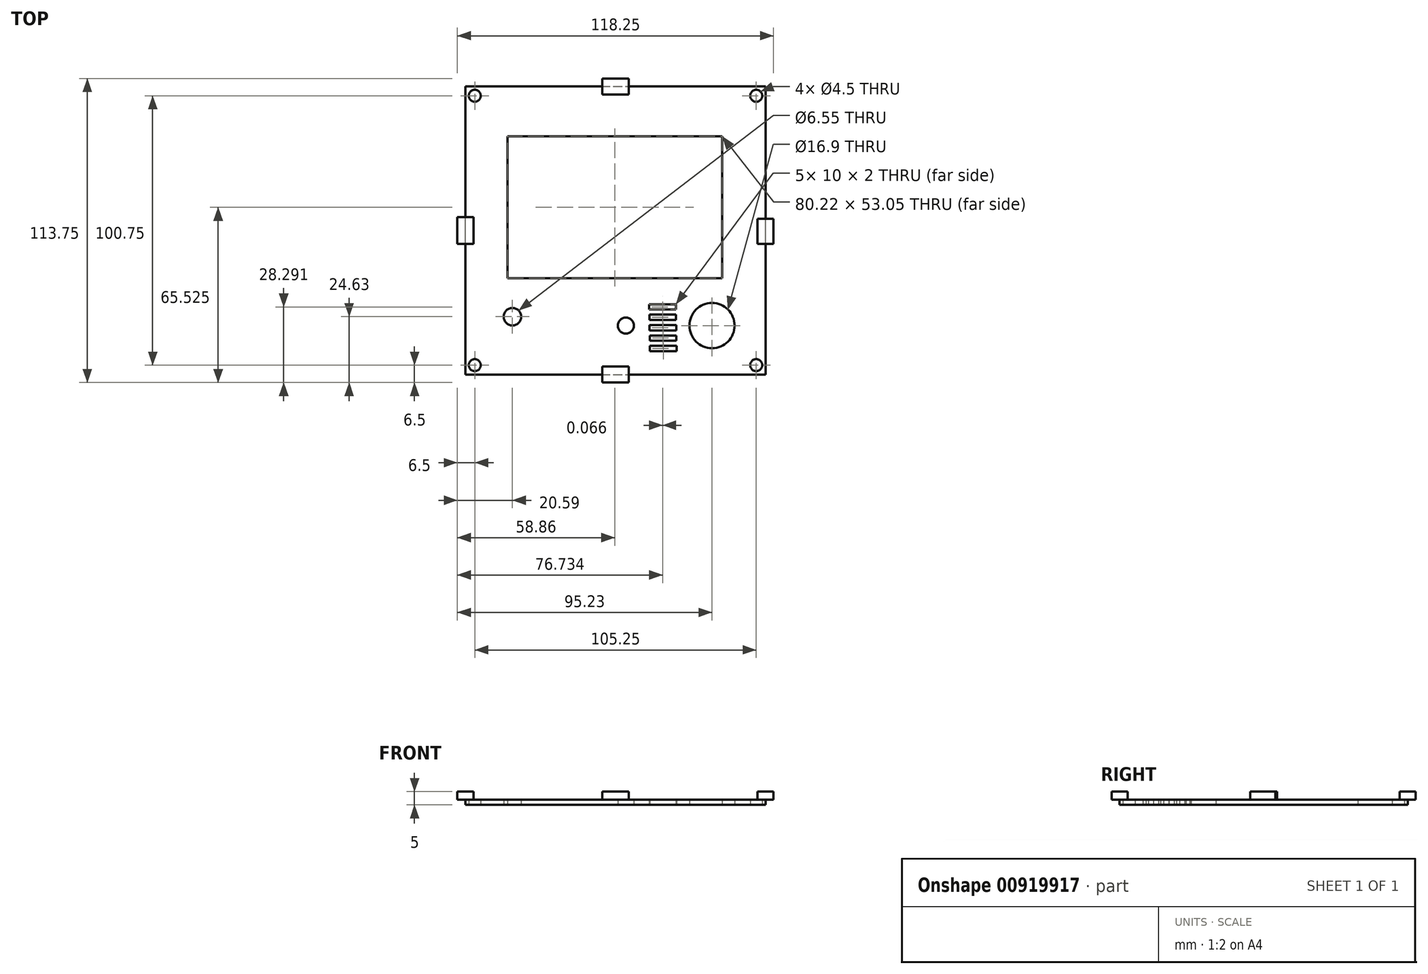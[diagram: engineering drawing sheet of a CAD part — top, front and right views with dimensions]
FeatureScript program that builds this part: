
annotation { "Feature Type Name" : "Feature", "Feature Type Description" : "" }
export const myFeature = defineFeature(function(context is Context, id is Id, definition is map)
    precondition{}
    {
        {
            var Q0;
            Q0=qCreatedBy(makeId("Top.planeOp"),FACE);
            var sketch = newSketch(context, id + "F0", { "sketchPlane" : qUnion([Q0])});
            skLineSegment(sketch, "E0.bottom", {"start": v(0, 0) * mm, "end": v(112.25, 0) * mm});
            skLineSegment(sketch, "E0.top", {"start": v(0, 107.75) * mm, "end": v(112.25, 107.75) * mm});
            skLineSegment(sketch, "E0.left", {"start": v(0, 0) * mm, "end": v(0, 107.75) * mm});
            skLineSegment(sketch, "E0.right", {"start": v(112.25, 0) * mm, "end": v(112.25, 107.75) * mm});
            skCircle(sketch, "E1", {"center": v(3.5, 104.25) * mm, "radius": 2.25 * mm});
            skCircle(sketch, "E2", {"center": v(108.75, 104.25) * mm, "radius": 2.25 * mm});
            skCircle(sketch, "E3", {"center": v(3.5, 3.5) * mm, "radius": 2.25 * mm});
            skCircle(sketch, "E4", {"center": v(108.75, 3.5) * mm, "radius": 2.25 * mm});
            skLineSegment(sketch, "E5.bottom", {"start": v(15.75, 89.05) * mm, "end": v(95.97, 89.05) * mm});
            skLineSegment(sketch, "E5.top", {"start": v(15.75, 36) * mm, "end": v(95.97, 36) * mm});
            skLineSegment(sketch, "E5.left", {"start": v(15.75, 89.05) * mm, "end": v(15.75, 36) * mm});
            skLineSegment(sketch, "E5.right", {"start": v(95.97, 89.05) * mm, "end": v(95.97, 36) * mm});
            skCircle(sketch, "E6", {"center": v(92.23, 18.3) * mm, "radius": 8.45 * mm});
            skCircle(sketch, "E7", {"center": v(60, 18.3) * mm, "radius": 3 * mm});
            skCircle(sketch, "E8", {"center": v(17.59, 21.63) * mm, "radius": 3.28 * mm});
            skLineSegment(sketch, "E9.bottom", {"start": v(68.73, 26.3) * mm, "end": v(78.73, 26.3) * mm});
            skLineSegment(sketch, "E9.top", {"start": v(68.73, 24.3) * mm, "end": v(78.73, 24.3) * mm});
            skLineSegment(sketch, "E9.left", {"start": v(68.73, 26.3) * mm, "end": v(68.73, 24.3) * mm});
            skLineSegment(sketch, "E9.right", {"start": v(78.73, 26.3) * mm, "end": v(78.73, 24.3) * mm});
            skLineSegment(sketch, "E10.1.0.0", {"start": v(78.8, 22.4) * mm, "end": v(78.8, 20.4) * mm});
            skLineSegment(sketch, "E10.1.0.1", {"start": v(68.8, 22.4) * mm, "end": v(68.8, 20.4) * mm});
            skLineSegment(sketch, "E10.1.0.2", {"start": v(68.8, 22.4) * mm, "end": v(78.8, 22.4) * mm});
            skLineSegment(sketch, "E10.1.0.3", {"start": v(68.8, 20.4) * mm, "end": v(78.8, 20.4) * mm});
            skLineSegment(sketch, "E10.2.0.0", {"start": v(78.87, 18.5) * mm, "end": v(78.87, 16.5) * mm});
            skLineSegment(sketch, "E10.2.0.1", {"start": v(68.87, 18.5) * mm, "end": v(68.87, 16.5) * mm});
            skLineSegment(sketch, "E10.2.0.2", {"start": v(68.87, 18.5) * mm, "end": v(78.87, 18.5) * mm});
            skLineSegment(sketch, "E10.2.0.3", {"start": v(68.87, 16.5) * mm, "end": v(78.87, 16.5) * mm});
            skLineSegment(sketch, "E10.3.0.0", {"start": v(78.93, 14.62) * mm, "end": v(78.93, 12.62) * mm});
            skLineSegment(sketch, "E10.3.0.1", {"start": v(68.93, 14.62) * mm, "end": v(68.93, 12.62) * mm});
            skLineSegment(sketch, "E10.3.0.2", {"start": v(68.93, 14.62) * mm, "end": v(78.93, 14.62) * mm});
            skLineSegment(sketch, "E10.3.0.3", {"start": v(68.93, 12.62) * mm, "end": v(78.93, 12.62) * mm});
            skLineSegment(sketch, "E10.4.0.0", {"start": v(79, 10.73) * mm, "end": v(79, 8.73) * mm});
            skLineSegment(sketch, "E10.4.0.1", {"start": v(69, 10.73) * mm, "end": v(69, 8.73) * mm});
            skLineSegment(sketch, "E10.4.0.2", {"start": v(69, 10.73) * mm, "end": v(79, 10.73) * mm});
            skLineSegment(sketch, "E10.4.0.3", {"start": v(69, 8.73) * mm, "end": v(79, 8.73) * mm});
            skLineSegment(sketch, "E10.direction1", {"start": v(68.73, 24.3) * mm, "end": v(68.8, 20.4) * mm, "construction": true});
            skSolve(sketch);
        }
        {
            var Q0;
            Q0=qSketchRegion(id+"F0",true);
            extrude(context, id + "F1", {"entities" : qUnion([Q0]), "depth" : 2 * mm, "offsetDistance" : 25 * mm});
        }
        {
            var Q0;
            Q0=makeQuery(id+"F1.opExtrude","CAP_FACE",FACE,{"disambiguationData":[OSD([sQuery(id+"F0.wireOp",EDGE,"E0.bottom"),sQuery(id+"F0.wireOp",EDGE,"E0.top"),sQuery(id+"F0.wireOp",EDGE,"E0.left"),sQuery(id+"F0.wireOp",EDGE,"E0.right"),sQuery(id+"F0.wireOp",EDGE,"E1"),sQuery(id+"F0.wireOp",EDGE,"E2"),sQuery(id+"F0.wireOp",EDGE,"E3"),sQuery(id+"F0.wireOp",EDGE,"E4"),sQuery(id+"F0.wireOp",EDGE,"E5.bottom"),sQuery(id+"F0.wireOp",EDGE,"E5.top"),sQuery(id+"F0.wireOp",EDGE,"E5.left"),sQuery(id+"F0.wireOp",EDGE,"E5.right"),sQuery(id+"F0.wireOp",EDGE,"E6"),sQuery(id+"F0.wireOp",EDGE,"E7"),sQuery(id+"F0.wireOp",EDGE,"E8"),sQuery(id+"F0.wireOp",EDGE,"E9.bottom"),sQuery(id+"F0.wireOp",EDGE,"E9.top"),sQuery(id+"F0.wireOp",EDGE,"E9.left"),sQuery(id+"F0.wireOp",EDGE,"E9.right"),sQuery(id+"F0.wireOp",EDGE,"E10.1.0.0"),sQuery(id+"F0.wireOp",EDGE,"E10.1.0.1"),sQuery(id+"F0.wireOp",EDGE,"E10.1.0.2"),sQuery(id+"F0.wireOp",EDGE,"E10.1.0.3"),sQuery(id+"F0.wireOp",EDGE,"E10.2.0.0"),sQuery(id+"F0.wireOp",EDGE,"E10.2.0.1"),sQuery(id+"F0.wireOp",EDGE,"E10.2.0.2"),sQuery(id+"F0.wireOp",EDGE,"E10.2.0.3"),sQuery(id+"F0.wireOp",EDGE,"E10.3.0.0"),sQuery(id+"F0.wireOp",EDGE,"E10.3.0.1"),sQuery(id+"F0.wireOp",EDGE,"E10.3.0.2"),sQuery(id+"F0.wireOp",EDGE,"E10.3.0.3"),sQuery(id+"F0.wireOp",EDGE,"E10.4.0.0"),sQuery(id+"F0.wireOp",EDGE,"E10.4.0.1"),sQuery(id+"F0.wireOp",EDGE,"E10.4.0.2"),sQuery(id+"F0.wireOp",EDGE,"E10.4.0.3")])],"isStart":false});
            var sketch = newSketch(context, id + "F2", { "sketchPlane" : qUnion([Q0])});
            skLineSegment(sketch, "E11.bottom", {"start": v(109.25, 58.25) * mm, "end": v(115.25, 58.25) * mm});
            skLineSegment(sketch, "E11.top", {"start": v(109.25, 48.87) * mm, "end": v(115.25, 48.87) * mm});
            skLineSegment(sketch, "E11.left", {"start": v(109.25, 58.25) * mm, "end": v(109.25, 48.87) * mm});
            skLineSegment(sketch, "E11.right", {"start": v(115.25, 58.25) * mm, "end": v(115.25, 48.87) * mm});
            skLineSegment(sketch, "E12.bottom", {"start": v(-3, 58.87) * mm, "end": v(3, 58.87) * mm});
            skLineSegment(sketch, "E12.top", {"start": v(-3, 48.87) * mm, "end": v(3, 48.87) * mm});
            skLineSegment(sketch, "E12.left", {"start": v(-3, 58.87) * mm, "end": v(-3, 48.87) * mm});
            skLineSegment(sketch, "E12.right", {"start": v(3, 58.87) * mm, "end": v(3, 48.87) * mm});
            skLineSegment(sketch, "E13.bottom", {"start": v(51.13, 110.75) * mm, "end": v(61.13, 110.75) * mm});
            skLineSegment(sketch, "E13.top", {"start": v(51.13, 104.75) * mm, "end": v(61.13, 104.75) * mm});
            skLineSegment(sketch, "E13.left", {"start": v(51.13, 110.75) * mm, "end": v(51.13, 104.75) * mm});
            skLineSegment(sketch, "E13.right", {"start": v(61.13, 110.75) * mm, "end": v(61.13, 104.75) * mm});
            skLineSegment(sketch, "E14.bottom", {"start": v(51.13, 3) * mm, "end": v(61.13, 3) * mm});
            skLineSegment(sketch, "E14.top", {"start": v(51.13, -3) * mm, "end": v(61.13, -3) * mm});
            skLineSegment(sketch, "E14.left", {"start": v(51.13, 3) * mm, "end": v(51.13, -3) * mm});
            skLineSegment(sketch, "E14.right", {"start": v(61.13, 3) * mm, "end": v(61.13, -3) * mm});
            skSolve(sketch);
        }
        {
            var Q0;
            Q0=qSketchRegion(id+"F2",true);
            extrude(context, id + "F3", {"entities" : qUnion([Q0]), "operationType" : NewBodyOperationType.ADD, "depth" : 3 * mm, "offsetDistance" : 25 * mm});
        }
    });
